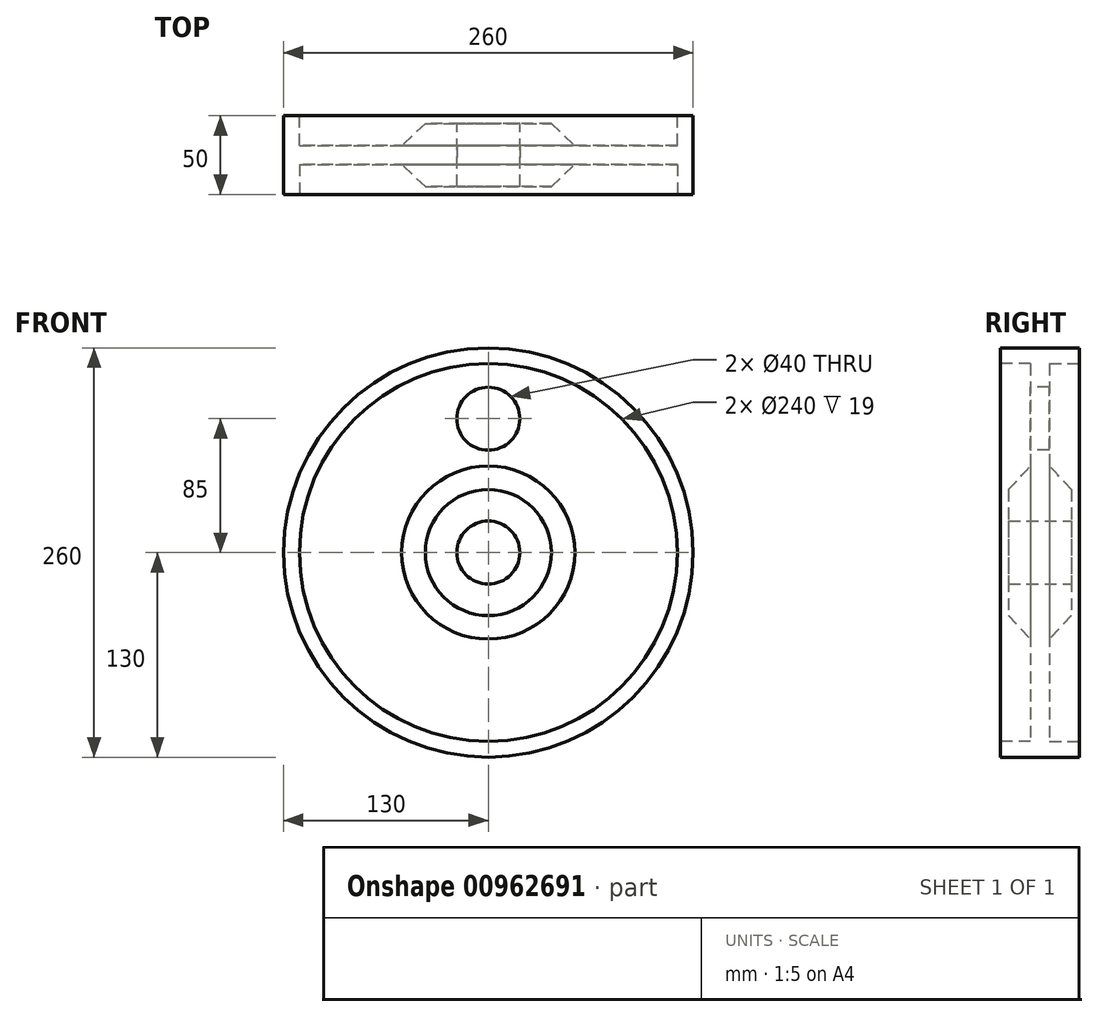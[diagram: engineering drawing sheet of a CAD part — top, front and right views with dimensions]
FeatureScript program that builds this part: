
annotation { "Feature Type Name" : "Feature", "Feature Type Description" : "" }
export const myFeature = defineFeature(function(context is Context, id is Id, definition is map)
    precondition{}
    {
        {
            var Q0;
            Q0=qCreatedBy(makeId("Right.planeOp"),FACE);
            var sketch = newSketch(context, id + "F0", { "sketchPlane" : qUnion([Q0])});
            skLineSegment(sketch, "E0", {"start": v(0, 130) * mm, "end": v(25, 130) * mm});
            skLineSegment(sketch, "E1", {"start": v(25, 130) * mm, "end": v(25, 120) * mm});
            skLineSegment(sketch, "E2", {"start": v(25, 120) * mm, "end": v(6, 120) * mm});
            skLineSegment(sketch, "E3", {"start": v(6, 120) * mm, "end": v(6, 55) * mm});
            skLineSegment(sketch, "E4", {"start": v(6, 55) * mm, "end": v(20, 40) * mm});
            skLineSegment(sketch, "E5", {"start": v(20, 40) * mm, "end": v(20, 20) * mm});
            skLineSegment(sketch, "E6", {"start": v(20, 20) * mm, "end": v(0, 20) * mm});
            skLineSegment(sketch, "E7", {"start": v(0, 20) * mm, "end": v(0, 130) * mm});
            skSolve(sketch);
        }
        {
            var Q0;
            Q0=qCreatedBy(makeId("Right.planeOp"),FACE);
            var sketch = newSketch(context, id + "F1", { "sketchPlane" : qUnion([Q0])});
            skLineSegment(sketch, "E8", {"start": v(0, 0) * mm, "end": v(0, 75.11) * mm, "construction": true});
            skLineSegment(sketch, "E9", {"start": v(0, 75.11) * mm, "end": v(0, -74.95) * mm, "construction": true});
            skSolve(sketch);
        }
        {
            var Q0;
            Q0=qCreatedBy(makeId("Right.planeOp"),FACE);
            var sketch = newSketch(context, id + "F2", { "sketchPlane" : qUnion([Q0])});
            skLineSegment(sketch, "E10", {"start": v(0, 0) * mm, "end": v(76.07, 0) * mm, "construction": true});
            skLineSegment(sketch, "E11", {"start": v(76.07, 0) * mm, "end": v(-75.69, 0) * mm, "construction": true});
            skSolve(sketch);
        }
        {
            var Q0;
            Q0=makeQuery(id+"F0.imprint","IMPRINT",FACE,{"disambiguationData":[TD([[makeQuery(id+"F0.imprint","IMPRINT",EDGE,{"derivedFrom":sQuery(id+"F0.wireOp",EDGE,"E0")}),-1.0]])]});
            var Q1;
            Q1=sQuery(id+"F2.wireOp",EDGE,"E11");
            revolve(context, id + "F3", {"surfaceOperationType" : NewSurfaceOperationType.NEW, "entities" : qUnion([Q0]), "axis" : qUnion([Q1]), "revolveType" : RevolveType.FULL});
        }
        {
            var Q0;
            Q0=makeQuery(id+"F3.opRevolve","SWEPT_BODY",BODY,{"disambiguationData":[OSD([sQuery(id+"F0.wireOp",EDGE,"E0"),sQuery(id+"F0.wireOp",EDGE,"E1"),sQuery(id+"F0.wireOp",EDGE,"E2"),sQuery(id+"F0.wireOp",EDGE,"E3"),sQuery(id+"F0.wireOp",EDGE,"E4"),sQuery(id+"F0.wireOp",EDGE,"E5"),sQuery(id+"F0.wireOp",EDGE,"E6"),sQuery(id+"F0.wireOp",EDGE,"E7")])]});
            var Q1;
            Q1=qCreatedBy(makeId("Front.planeOp"),FACE);
            mirror(context, id + "F4", {"operationType" : NewBodyOperationType.ADD, "entities" : qUnion([Q0]), "mirrorPlane" : qUnion([Q1])});
        }
        {
            var Q0;
            Q0=makeQuery(id+"F4.opPattern","COPY",FACE,{"derivedFrom":makeQuery(id+"F3.opRevolve","SWEPT_FACE",FACE,{"disambiguationData":[OSD([sQuery(id+"F0.wireOp",EDGE,"E3")])]}),"instanceName":"1"});
            var sketch = newSketch(context, id + "F5", { "sketchPlane" : qUnion([Q0])});
            skPoint(sketch, "E12", {"position": v(0, 85) * mm});
            skCircle(sketch, "E13", {"center": v(0, 85) * mm, "radius": 20 * mm});
            skSolve(sketch);
        }
        {
            var Q0;
            Q0=makeQuery(id+"F5.imprint","IMPRINT",FACE,{"disambiguationData":[TD([[makeQuery(id+"F5.imprint","IMPRINT",EDGE,{"derivedFrom":sQuery(id+"F5.wireOp",EDGE,"E13")}),1.0]])]});
            extrude(context, id + "F6", {"entities" : qUnion([Q0]), "operationType" : NewBodyOperationType.REMOVE, "oppositeDirection" : true, "depth" : 25 * mm, "offsetDistance" : 25 * mm});
        }
    });
